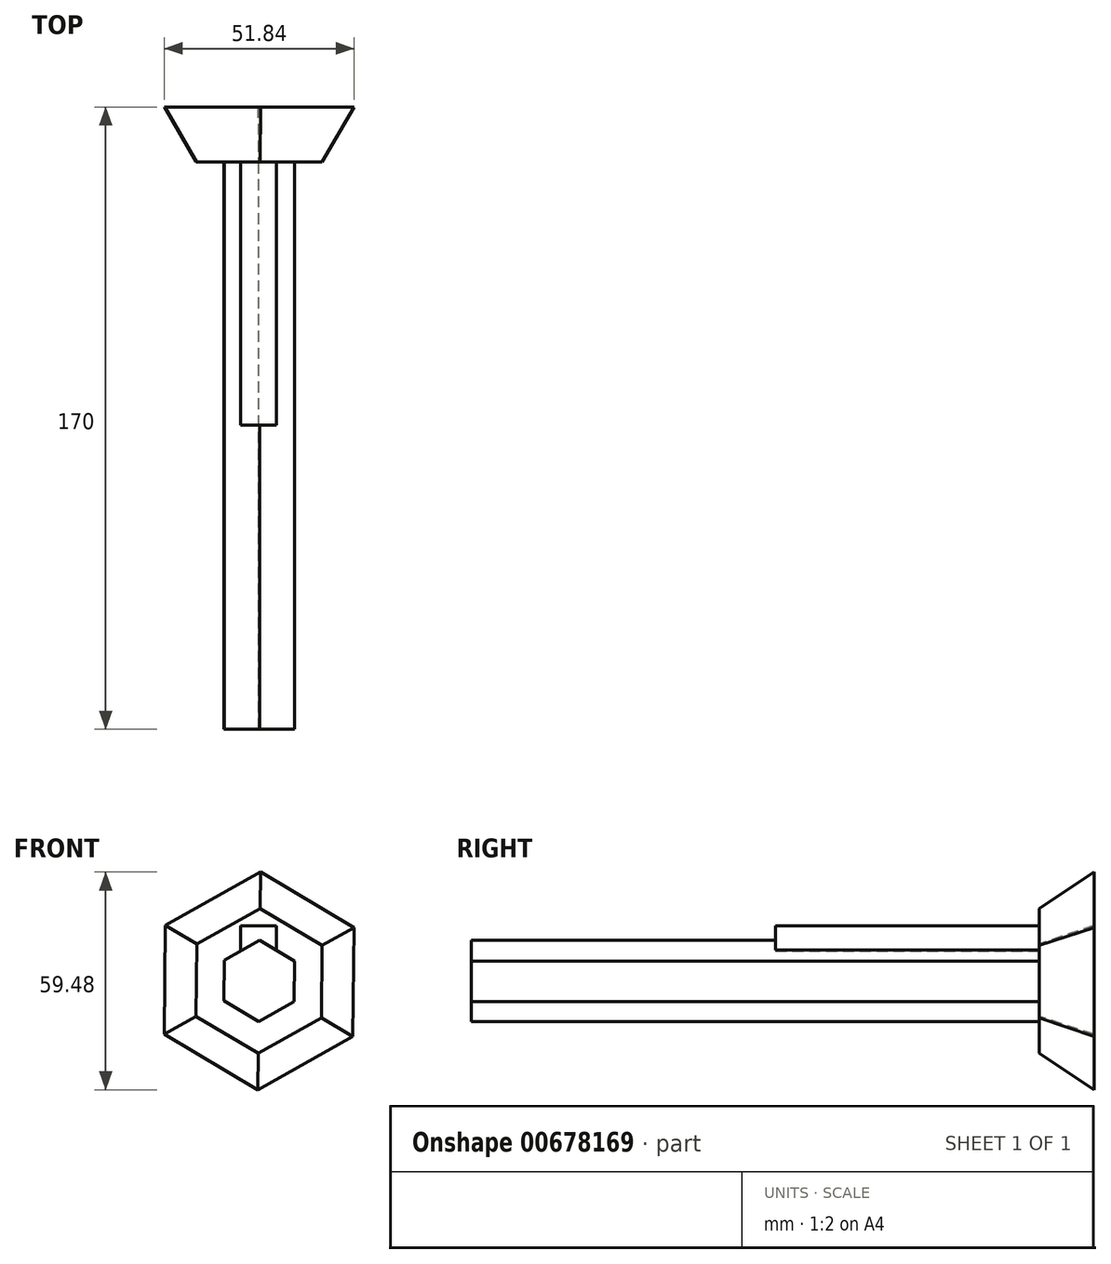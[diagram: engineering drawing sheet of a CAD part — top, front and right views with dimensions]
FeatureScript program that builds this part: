
annotation { "Feature Type Name" : "Feature", "Feature Type Description" : "" }
export const myFeature = defineFeature(function(context is Context, id is Id, definition is map)
    precondition{}
    {
        {
            var Q0;
            Q0=qCreatedBy(makeId("Front.planeOp"),FACE);
            var sketch = newSketch(context, id + "F0", { "sketchPlane" : qUnion([Q0])});
            skLineSegment(sketch, "E0.0", {"start": v(9.57, -5.67) * mm, "end": v(-0.13, -11.12) * mm});
            skLineSegment(sketch, "E0.1", {"start": v(-0.13, -11.12) * mm, "end": v(-9.7, -5.45) * mm});
            skLineSegment(sketch, "E0.2", {"start": v(-9.7, -5.45) * mm, "end": v(-9.57, 5.67) * mm});
            skLineSegment(sketch, "E0.3", {"start": v(-9.57, 5.67) * mm, "end": v(0.13, 11.12) * mm});
            skLineSegment(sketch, "E0.4", {"start": v(0.13, 11.12) * mm, "end": v(9.7, 5.45) * mm});
            skLineSegment(sketch, "E0.5", {"start": v(9.7, 5.45) * mm, "end": v(9.57, -5.67) * mm});
            skSolve(sketch);
        }
        {
            var Q0;
            Q0=makeQuery(id+"F0.imprint","IMPRINT",FACE,{"disambiguationData":[TD([[makeQuery(id+"F0.imprint","IMPRINT",EDGE,{"derivedFrom":sQuery(id+"F0.wireOp",EDGE,"E0.0")}),-1.0]])]});
            var Q1;
            Q1=sQuery(id+"F0.wireOp",EDGE,"E0.0");
            var Q2;
            Q2=sQuery(id+"F0.wireOp",EDGE,"E0.1");
            var Q3;
            Q3=sQuery(id+"F0.wireOp",EDGE,"E0.2");
            var Q4;
            Q4=sQuery(id+"F0.wireOp",EDGE,"E0.3");
            var Q5;
            Q5=sQuery(id+"F0.wireOp",EDGE,"E0.4");
            var Q6;
            Q6=sQuery(id+"F0.wireOp",EDGE,"E0.5");
            extrude(context, id + "F1", {"entities" : qUnion([Q0]), "surfaceEntities" : qUnion([Q1, Q2, Q3, Q4, Q5, Q6]), "depth" : 155 * mm, "offsetDistance" : 25 * mm, "symmetric" : true});
        }
        {
            var Q0;
            Q0=makeQuery(id+"F1.opExtrude","CAP_FACE",FACE,{"disambiguationData":[OSD([sQuery(id+"F0.wireOp",EDGE,"E0.0"),sQuery(id+"F0.wireOp",EDGE,"E0.1"),sQuery(id+"F0.wireOp",EDGE,"E0.2"),sQuery(id+"F0.wireOp",EDGE,"E0.3"),sQuery(id+"F0.wireOp",EDGE,"E0.4"),sQuery(id+"F0.wireOp",EDGE,"E0.5")])],"isStart":true});
            var sketch = newSketch(context, id + "F2", { "sketchPlane" : qUnion([Q0])});
            skCircle(sketch, "E1.cCircle", {"center": v(0, 0) * mm, "radius": 17.1 * mm, "construction": true});
            skLineSegment(sketch, "E1.0", {"start": v(17.2, -9.68) * mm, "end": v(0.22, -19.74) * mm});
            skLineSegment(sketch, "E1.1", {"start": v(0.22, -19.74) * mm, "end": v(-16.98, -10.06) * mm});
            skLineSegment(sketch, "E1.2", {"start": v(-16.98, -10.06) * mm, "end": v(-17.2, 9.68) * mm});
            skLineSegment(sketch, "E1.3", {"start": v(-17.2, 9.68) * mm, "end": v(-0.22, 19.74) * mm});
            skLineSegment(sketch, "E1.4", {"start": v(-0.22, 19.74) * mm, "end": v(16.98, 10.06) * mm});
            skLineSegment(sketch, "E1.5", {"start": v(16.98, 10.06) * mm, "end": v(17.2, -9.68) * mm});
            skPoint(sketch, "E1.0.midPoint", {"position": v(8.71, -14.7) * mm});
            skSolve(sketch);
        }
        {
            var Q0;
            Q0=makeQuery(id+"F2.imprint","IMPRINT",FACE,{"disambiguationData":[TD([[makeQuery(id+"F2.imprint","IMPRINT",EDGE,{"derivedFrom":sQuery(id+"F2.wireOp",EDGE,"E1.0")}),-1.0]])]});
            var Q1;
            Q1=makeQuery(id+"F2.imprint","IMPRINT",FACE,{"disambiguationData":[TD([[makeQuery(id+"F2.imprint","IMPRINT",EDGE,{"derivedFrom":makeQuery(id+"F1.opExtrude","CAP_EDGE",EDGE,{"disambiguationData":[OSD([sQuery(id+"F0.wireOp",EDGE,"E0.0")])],"isStart":true})}),1.0]])]});
            extrude(context, id + "F3", {"entities" : qUnion([Q0, Q1]), "operationType" : NewBodyOperationType.ADD, "depth" : 15 * mm, "offsetDistance" : 25 * mm, "hasDraft" : true, "draftAngle" : 30 * degree});
        }
        {
            var Q0;
            Q0=qCreatedBy(makeId("Top.planeOp"),FACE);
            var sketch = newSketch(context, id + "F4", { "sketchPlane" : qUnion([Q0])});
            skLineSegment(sketch, "E2.bottom", {"start": v(-5.02, 86.99) * mm, "end": v(4.7, 86.99) * mm});
            skLineSegment(sketch, "E2.top", {"start": v(-5.02, 5.6) * mm, "end": v(4.7, 5.6) * mm});
            skLineSegment(sketch, "E2.left", {"start": v(-5.02, 86.99) * mm, "end": v(-5.02, 5.6) * mm});
            skLineSegment(sketch, "E2.right", {"start": v(4.7, 86.99) * mm, "end": v(4.7, 5.6) * mm});
            skSolve(sketch);
        }
        {
            var Q0;
            Q0 = qSketchRegion(id + "F4", true);
            extrude(context, id + "F5", {"entities" : qUnion([Q0]), "operationType" : NewBodyOperationType.ADD, "depth" : 15 * mm, "offsetDistance" : 25 * mm});
        }
    });
